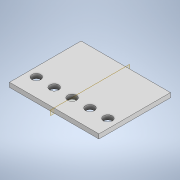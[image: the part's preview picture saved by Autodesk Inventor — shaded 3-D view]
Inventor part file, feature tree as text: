
AUTODESK INVENTOR PART (.ipt)
format: ipt  version: 2020.2 (Build 242310000, 310)  size: 125,952 bytes
history: native  units: in
note: dims shown in document units (in); Inventor stores cm internally (conversion verified against a paired STEP export)
features: extrude x2, sketch x2
ambient origin geometry x8: Origin, YZ Plane, XZ Plane, XY Plane, X Axis, Y Axis, Z Axis, Center Point
bodies: Solid1 (feature_tree)
feature tree (4):
  extrude  "Extrusion1"  Depth=0.25in
  extrude  "Extrusion2"  Depth=5.0in
  sketch  "Sketch1"  dims[d0=0.25in d1=0.0in d2=3.0in]
  sketch  "Sketch3"  dims[d3=4.0in d4=0.5in d5=0.5in d6=1.9685in d8=1.0in d9=0.3937in d11=1.0in d13=5.0in d14=0.0in d15=0.0in]
